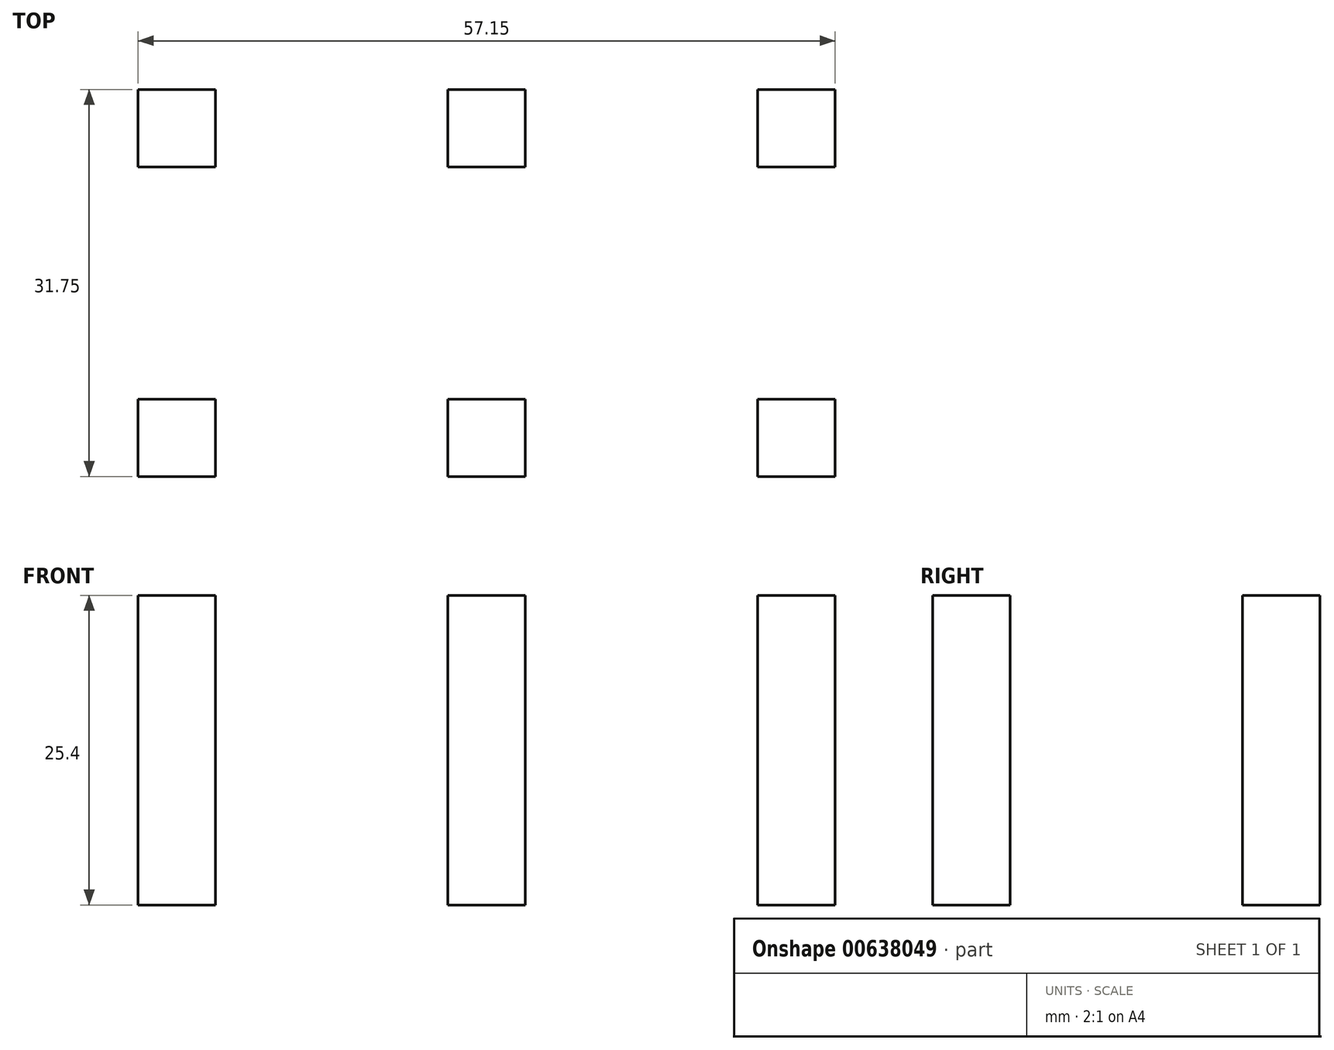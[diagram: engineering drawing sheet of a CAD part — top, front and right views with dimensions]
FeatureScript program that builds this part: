
annotation { "Feature Type Name" : "Feature", "Feature Type Description" : "" }
export const myFeature = defineFeature(function(context is Context, id is Id, definition is map)
    precondition{}
    {
        {
            var Q0;
            Q0=qCreatedBy(makeId("Top.planeOp"),FACE);
            var sketch = newSketch(context, id + "F0", { "sketchPlane" : qUnion([Q0])});
            skLineSegment(sketch, "E0.bottom", {"start": v(0, 0) * mm, "end": v(-6.35, 0) * mm});
            skLineSegment(sketch, "E0.top", {"start": v(0, -6.35) * mm, "end": v(-6.35, -6.35) * mm});
            skLineSegment(sketch, "E0.left", {"start": v(0, 0) * mm, "end": v(0, -6.35) * mm});
            skLineSegment(sketch, "E0.right", {"start": v(-6.35, 0) * mm, "end": v(-6.35, -6.35) * mm});
            skLineSegment(sketch, "E1", {"start": v(-6.35, 0) * mm, "end": v(-25.4, 0) * mm});
            skLineSegment(sketch, "E2.0.1.0", {"start": v(0, 25.4) * mm, "end": v(0, 19.05) * mm});
            skLineSegment(sketch, "E2.0.1.1", {"start": v(0, 19.05) * mm, "end": v(-6.35, 19.05) * mm});
            skLineSegment(sketch, "E2.0.1.2", {"start": v(-6.35, 25.4) * mm, "end": v(-6.35, 19.05) * mm});
            skLineSegment(sketch, "E2.0.1.3", {"start": v(0, 25.4) * mm, "end": v(-6.35, 25.4) * mm});
            skLineSegment(sketch, "E2.0.1.4", {"start": v(-6.35, 25.4) * mm, "end": v(-25.4, 25.4) * mm});
            skLineSegment(sketch, "E2.1.0.0", {"start": v(-25.4, 0) * mm, "end": v(-25.4, -6.35) * mm});
            skLineSegment(sketch, "E2.1.0.1", {"start": v(-25.4, -6.35) * mm, "end": v(-31.75, -6.35) * mm});
            skLineSegment(sketch, "E2.1.0.2", {"start": v(-31.75, 0) * mm, "end": v(-31.75, -6.35) * mm});
            skLineSegment(sketch, "E2.1.0.3", {"start": v(-25.4, 0) * mm, "end": v(-31.75, 0) * mm});
            skLineSegment(sketch, "E2.1.0.4", {"start": v(-31.75, 0) * mm, "end": v(-50.8, 0) * mm});
            skLineSegment(sketch, "E2.1.1.0", {"start": v(-25.4, 25.4) * mm, "end": v(-25.4, 19.05) * mm});
            skLineSegment(sketch, "E2.1.1.1", {"start": v(-25.4, 19.05) * mm, "end": v(-31.75, 19.05) * mm});
            skLineSegment(sketch, "E2.1.1.2", {"start": v(-31.75, 25.4) * mm, "end": v(-31.75, 19.05) * mm});
            skLineSegment(sketch, "E2.1.1.3", {"start": v(-25.4, 25.4) * mm, "end": v(-31.75, 25.4) * mm});
            skLineSegment(sketch, "E2.1.1.4", {"start": v(-31.75, 25.4) * mm, "end": v(-50.8, 25.4) * mm});
            skLineSegment(sketch, "E2.2.0.0", {"start": v(-50.8, 0) * mm, "end": v(-50.8, -6.35) * mm});
            skLineSegment(sketch, "E2.2.0.1", {"start": v(-50.8, -6.35) * mm, "end": v(-57.15, -6.35) * mm});
            skLineSegment(sketch, "E2.2.0.2", {"start": v(-57.15, 0) * mm, "end": v(-57.15, -6.35) * mm});
            skLineSegment(sketch, "E2.2.0.3", {"start": v(-50.8, 0) * mm, "end": v(-57.15, 0) * mm});
            skLineSegment(sketch, "E2.2.0.4", {"start": v(-57.15, 0) * mm, "end": v(-76.2, 0) * mm});
            skLineSegment(sketch, "E2.2.1.0", {"start": v(-50.8, 25.4) * mm, "end": v(-50.8, 19.05) * mm});
            skLineSegment(sketch, "E2.2.1.1", {"start": v(-50.8, 19.05) * mm, "end": v(-57.15, 19.05) * mm});
            skLineSegment(sketch, "E2.2.1.2", {"start": v(-57.15, 25.4) * mm, "end": v(-57.15, 19.05) * mm});
            skLineSegment(sketch, "E2.2.1.3", {"start": v(-50.8, 25.4) * mm, "end": v(-57.15, 25.4) * mm});
            skLineSegment(sketch, "E2.2.1.4", {"start": v(-57.15, 25.4) * mm, "end": v(-76.2, 25.4) * mm});
            skLineSegment(sketch, "E2.direction1", {"start": v(0, 0) * mm, "end": v(-25.4, 0) * mm, "construction": true});
            skLineSegment(sketch, "E2.direction2", {"start": v(0, 0) * mm, "end": v(0, 25.4) * mm, "construction": true});
            skSolve(sketch);
        }
        {
            var Q0;
            Q0 = qSketchRegion(id + "F0", true);
            extrude(context, id + "F1", {"entities" : qUnion([Q0]), "depth" : 25.4 * mm, "offsetDistance" : 25.4 * mm});
        }
    });
